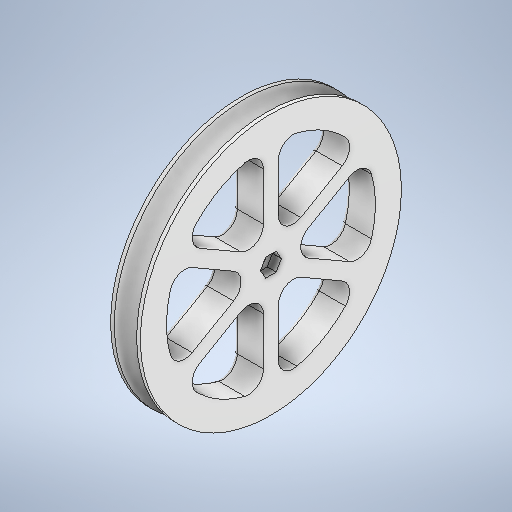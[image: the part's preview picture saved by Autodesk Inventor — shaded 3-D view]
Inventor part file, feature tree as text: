
AUTODESK INVENTOR PART (.ipt)
format: ipt  version: 2025.2 (Build 292293000, 293)  size: 576,000 bytes
history: native  units: mm
features: other x24, sketch x13, extrude x9, plane x4, fillet x4, pattern_circular x1, revolve x1
ambient origin geometry x8: Origin, YZ Plane, XZ Plane, XY Plane, X Axis, Y Axis, Z Axis, Center Point
bodies: Solid1 (feature_tree)
feature tree (56):
  extrude  "Extrusion1"  Depth=12.0mm
  extrude  "Extrusion2"  Depth=12.0mm
  extrude  "Extrusion3"  Depth=30.0mm
  extrude  "Extrusion4"  Depth=12.0mm
  extrude  "Extrusion5"  Depth=2.0mm
  sketch  "Sketch6"  dims[d14=4.0mm d15=0.0mm]
  other  "UCS1"
  plane  "Work Plane1"
  extrude  "Extrusion6"  Depth=10.0mm
  pattern_circular  "Circular Pattern1"  Count=2  [1 undecoded]
  fillet  "Fillet1"  [1 undecoded]
  extrude  "Extrusion7"  Depth=10.0mm
  fillet  "Fillet2"  Radius=60.0mm
  fillet  "Fillet3"  Radius=10.0mm
  plane  "Work Plane2"
  sketch  "Sketch11"  dims[d27=50.0mm d28=2.0mm d29=0.0mm d30=0.0mm d31=60.0mm d32=360.0deg d34=10.0mm]
  other  "UCS2"
  plane  "Work Plane3"
  sketch  "Sketch12"  dims[d37=160.0mm d38=10.0mm d39=0.0mm d40=10.0mm]
  sketch  "Sketch13"  dims[d41=2.5mm d42=175.0mm]
  plane  "Work Plane4"
  sketch  "Sketch14"  dims[d43=0.0mm d44=0.0mm d45=0.0mm d46=0.0mm d47=0.0mm d48=0.0mm d49=15.0mm]
  revolve  "Revolution1"  [1 undecoded]
  fillet  "Fillet5"  Radius=10.0mm
  sketch  "Sketch15"  dims[d50=7.5mm d51=360.0deg d53=7.5mm d54=0.15mm d55=0.1mm d56=0.0mm d57=0.0mm d58=0.0mm d59=0.0mm d60=5.0mm d61=0.0mm d62=0.0mm d63=0.0mm d64=0.0mm d65=0.0mm d66=0.0mm d35=0.0mm d36=0.0mm d52=0.872665mm]
  extrude  "Extrusion8"  Depth=2.5mm
  extrude  "Extrusion9"  Depth=15.0mm
  other  "UCS3"
  sketch  "Sketch1"  dims[d0=12.0mm d1=40.0mm]
  sketch  "Sketch2"  dims[d2=20.0mm d3=0.0mm d4=12.0mm]
  sketch  "Sketch3"  dims[d5=6.0mm d6=0.0mm d7=30.0mm]
  sketch  "Sketch4"  dims[d8=6.0mm d9=0.0mm d10=12.0mm]
  sketch  "Sketch5"  dims[d11=2.0mm d12=0.0mm d13=3.0mm]
  sketch  "Sketch7"  dims[d16=0.0mm d17=0.0mm d18=0.0mm d19=0.0mm d20=0.0mm d21=0.0mm d22=10.0mm d23=20.0mm d24=90.0deg]
  sketch  "Sketch9"  dims[d25=20.0mm d26=10.0mm]
  other  "UCS1: YZ Plane"
  other  "UCS1: XZ Plane"
  other  "UCS1: XY Plane"
  other  "UCS1: X Axis"
  other  "UCS1: Y Axis"
  other  "UCS1: Z Axis"
  other  "UCS1: Center Point"
  other  "UCS2: YZ Plane"
  other  "UCS2: XZ Plane"
  other  "UCS2: XY Plane"
  other  "UCS2: X Axis"
  other  "UCS2: Y Axis"
  other  "UCS2: Z Axis"
  other  "UCS2: Center Point"
  other  "UCS3: YZ Plane"
  other  "UCS3: XZ Plane"
  other  "UCS3: XY Plane"
  other  "UCS3: X Axis"
  other  "UCS3: Y Axis"
  other  "UCS3: Z Axis"
  other  "UCS3: Center Point"
note: 3 required parameter values undecoded (feature->parameter linkage not recoverable at this tier; creation-order binding heuristic only, values carry confidence <= 0.55)